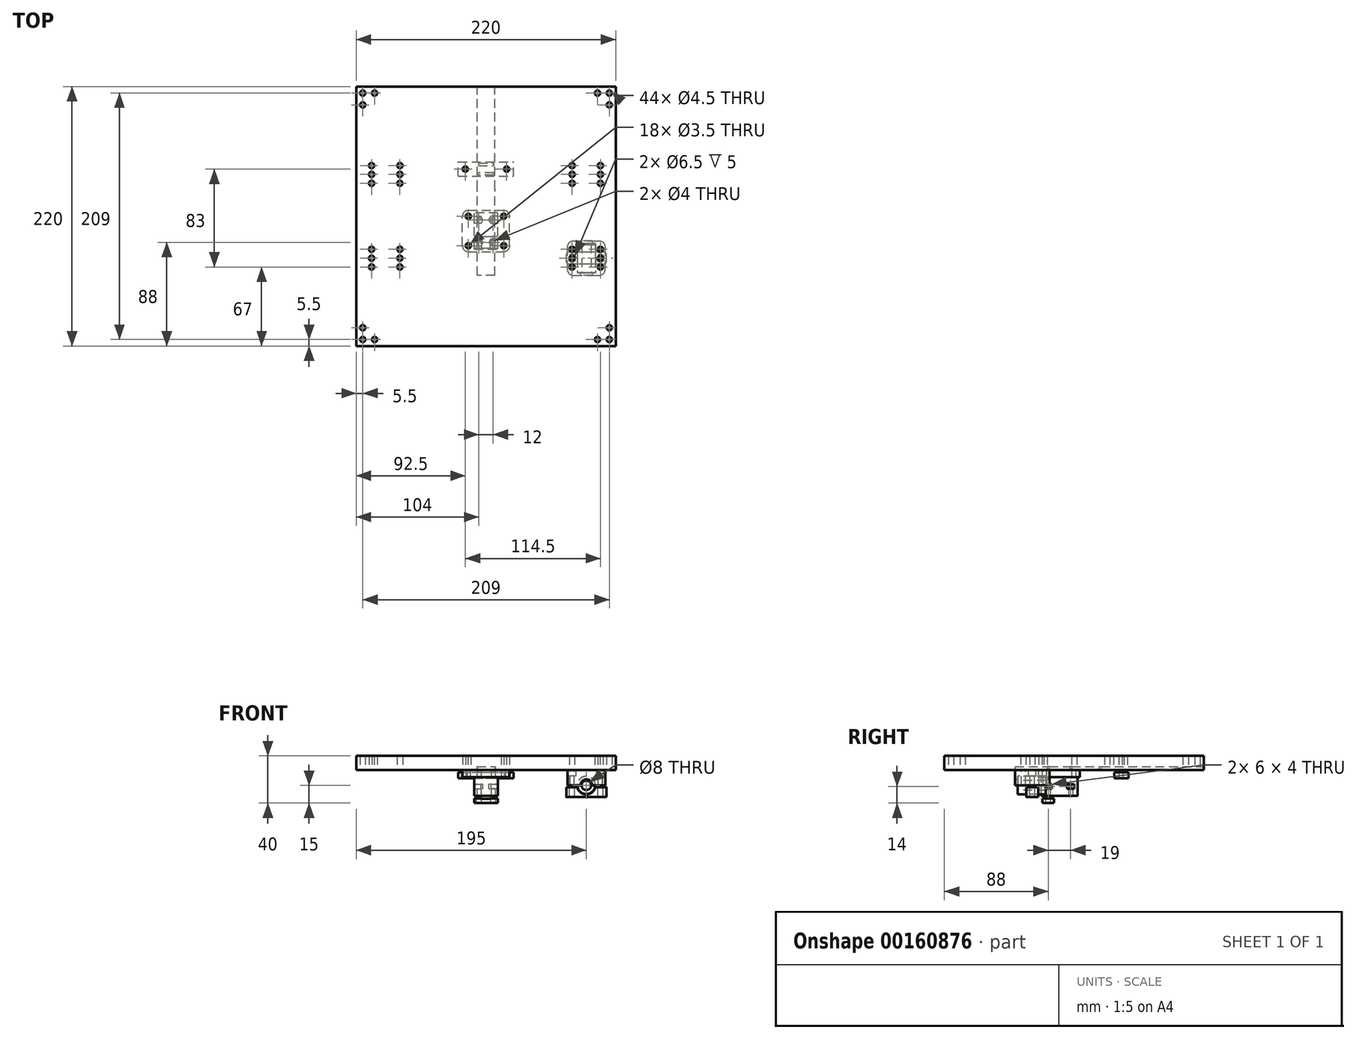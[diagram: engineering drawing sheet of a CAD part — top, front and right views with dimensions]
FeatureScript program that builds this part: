
annotation { "Feature Type Name" : "Feature", "Feature Type Description" : "" }
export const myFeature = defineFeature(function(context is Context, id is Id, definition is map)
    precondition{}
    {
        {
            var Q0;
            Q0=qCreatedBy(makeId("Top.planeOp"),FACE);
            var sketch = newSketch(context, id + "F0", { "sketchPlane" : qUnion([Q0])});
            skLineSegment(sketch, "E0.bottom", {"start": v(-110, 110) * mm, "end": v(110, 110) * mm});
            skLineSegment(sketch, "E0.top", {"start": v(-110, -110) * mm, "end": v(110, -110) * mm});
            skLineSegment(sketch, "E0.left", {"start": v(-110, 110) * mm, "end": v(-110, -110) * mm});
            skLineSegment(sketch, "E0.right", {"start": v(110, 110) * mm, "end": v(110, -110) * mm});
            skPoint(sketch, "E1", {"position": v(0, 110) * mm});
            skPoint(sketch, "E2", {"position": v(110, 0) * mm});
            skLineSegment(sketch, "E3", {"start": v(85, -48) * mm, "end": v(85, 0) * mm, "construction": true});
            skCircle(sketch, "E4", {"center": v(97, -43) * mm, "radius": 2.25 * mm});
            skLineSegment(sketch, "E5", {"start": v(85, -48) * mm, "end": v(92.5, -48) * mm, "construction": true});
            skLineSegment(sketch, "E6", {"start": v(92.5, -48) * mm, "end": v(92.5, -23) * mm, "construction": true});
            skLineSegment(sketch, "E7", {"start": v(92.5, -23) * mm, "end": v(77.5, -23) * mm, "construction": true});
            skLineSegment(sketch, "E8", {"start": v(77.5, -23) * mm, "end": v(77.5, -48) * mm, "construction": true});
            skLineSegment(sketch, "E9", {"start": v(77.5, -48) * mm, "end": v(85, -48) * mm, "construction": true});
            skLineSegment(sketch, "E10", {"start": v(77.5, -35.5) * mm, "end": v(92.5, -35.5) * mm, "construction": true});
            skCircle(sketch, "E11.MirrorC", {"center": v(97, -28) * mm, "radius": 2.25 * mm});
            skCircle(sketch, "E12.MirrorC", {"center": v(73, -28) * mm, "radius": 2.25 * mm});
            skCircle(sketch, "E13.MirrorC", {"center": v(73, -43) * mm, "radius": 2.25 * mm});
            skLineSegment(sketch, "E14", {"start": v(85, -48) * mm, "end": v(85, -50) * mm, "construction": true});
            skLineSegment(sketch, "E15.bottom", {"start": v(69, -50) * mm, "end": v(101, -50) * mm, "construction": true});
            skLineSegment(sketch, "E15.top", {"start": v(69, -21) * mm, "end": v(101, -21) * mm, "construction": true});
            skLineSegment(sketch, "E15.left", {"start": v(69, -50) * mm, "end": v(69, -21) * mm, "construction": true});
            skLineSegment(sketch, "E15.right", {"start": v(101, -50) * mm, "end": v(101, -21) * mm, "construction": true});
            skCircle(sketch, "E16", {"center": v(73, -35.5) * mm, "radius": 2.25 * mm});
            skCircle(sketch, "E17.MirrorC", {"center": v(97, -35.5) * mm, "radius": 2.25 * mm});
            skCircle(sketch, "E18.MirrorC", {"center": v(73, 28) * mm, "radius": 2.25 * mm});
            skCircle(sketch, "E19.MirrorC", {"center": v(73, 35.5) * mm, "radius": 2.25 * mm});
            skCircle(sketch, "E20.MirrorC", {"center": v(73, 43) * mm, "radius": 2.25 * mm});
            skCircle(sketch, "E21.MirrorC", {"center": v(97, 43) * mm, "radius": 2.25 * mm});
            skCircle(sketch, "E22.MirrorC", {"center": v(97, 35.5) * mm, "radius": 2.25 * mm});
            skCircle(sketch, "E23.MirrorC", {"center": v(97, 28) * mm, "radius": 2.25 * mm});
            skCircle(sketch, "E24.MirrorC", {"center": v(-73, 43) * mm, "radius": 2.25 * mm});
            skCircle(sketch, "E25.MirrorC", {"center": v(-73, 28) * mm, "radius": 2.25 * mm});
            skCircle(sketch, "E26.MirrorC", {"center": v(-97, 28) * mm, "radius": 2.25 * mm});
            skCircle(sketch, "E27.MirrorC", {"center": v(-97, 43) * mm, "radius": 2.25 * mm});
            skCircle(sketch, "E28.MirrorC", {"center": v(-73, 35.5) * mm, "radius": 2.25 * mm});
            skCircle(sketch, "E29.MirrorC", {"center": v(-97, 35.5) * mm, "radius": 2.25 * mm});
            skCircle(sketch, "E30.MirrorC", {"center": v(-73, -28) * mm, "radius": 2.25 * mm});
            skCircle(sketch, "E31.MirrorC", {"center": v(-73, -35.5) * mm, "radius": 2.25 * mm});
            skCircle(sketch, "E32.MirrorC", {"center": v(-73, -43) * mm, "radius": 2.25 * mm});
            skCircle(sketch, "E33.MirrorC", {"center": v(-97, -43) * mm, "radius": 2.25 * mm});
            skCircle(sketch, "E34.MirrorC", {"center": v(-97, -35.5) * mm, "radius": 2.25 * mm});
            skCircle(sketch, "E35.MirrorC", {"center": v(-97, -28) * mm, "radius": 2.25 * mm});
            skCircle(sketch, "E36", {"center": v(104.5, 104.5) * mm, "radius": 2.25 * mm});
            skCircle(sketch, "E37", {"center": v(104.5, 94.5) * mm, "radius": 2.25 * mm});
            skCircle(sketch, "E38.1.0", {"center": v(94.5, 104.5) * mm, "radius": 2.25 * mm});
            skLineSegment(sketch, "E38.anchor1", {"start": v(104.5, 104.5) * mm, "end": v(104.5, 94.5) * mm, "construction": true});
            skLineSegment(sketch, "E38.anchor2", {"start": v(104.5, 104.5) * mm, "end": v(94.5, 104.5) * mm, "construction": true});
            skCircle(sketch, "E39.MirrorC", {"center": v(104.5, -94.5) * mm, "radius": 2.25 * mm});
            skCircle(sketch, "E40.MirrorC", {"center": v(104.5, -104.5) * mm, "radius": 2.25 * mm});
            skCircle(sketch, "E41.MirrorC", {"center": v(94.5, -104.5) * mm, "radius": 2.25 * mm});
            skCircle(sketch, "E42.MirrorC", {"center": v(-94.5, -104.5) * mm, "radius": 2.25 * mm});
            skCircle(sketch, "E43.MirrorC", {"center": v(-104.5, -104.5) * mm, "radius": 2.25 * mm});
            skCircle(sketch, "E44.MirrorC", {"center": v(-104.5, -94.5) * mm, "radius": 2.25 * mm});
            skCircle(sketch, "E45.MirrorC", {"center": v(-104.5, 94.5) * mm, "radius": 2.25 * mm});
            skCircle(sketch, "E46.MirrorC", {"center": v(-104.5, 104.5) * mm, "radius": 2.25 * mm});
            skCircle(sketch, "E47.MirrorC", {"center": v(-94.5, 104.5) * mm, "radius": 2.25 * mm});
            skCircle(sketch, "E48.2.0.0", {"center": v(-17.5, 40) * mm, "radius": 2.25 * mm});
            skCircle(sketch, "E49.MirrorC", {"center": v(17.5, 40) * mm, "radius": 2.25 * mm});
            skCircle(sketch, "E50", {"center": v(-15, -25) * mm, "radius": 2.25 * mm});
            skCircle(sketch, "E51.MirrorC", {"center": v(15, -25) * mm, "radius": 2.25 * mm});
            skCircle(sketch, "E52", {"center": v(-15, 0) * mm, "radius": 2.25 * mm});
            skCircle(sketch, "E53.MirrorC", {"center": v(15, 0) * mm, "radius": 2.25 * mm});
            skSolve(sketch);
        }
        {
            var Q0;
            Q0 = qSketchRegion(id + "F0", true);
            extrude(context, id + "F1", {"entities" : qUnion([Q0]), "depth" : 12 * mm});
        }
        {
            var Q0;
            Q0=makeQuery(id+"F1.opExtrude","CAP_FACE",FACE,{"disambiguationData":[OSD([sQuery(id+"F0.wireOp",EDGE,"E0.bottom"),sQuery(id+"F0.wireOp",EDGE,"E0.top"),sQuery(id+"F0.wireOp",EDGE,"E0.left"),sQuery(id+"F0.wireOp",EDGE,"E0.right"),sQuery(id+"F0.wireOp",EDGE,"E4"),sQuery(id+"F0.wireOp",EDGE,"E11.MirrorC"),sQuery(id+"F0.wireOp",EDGE,"E12.MirrorC"),sQuery(id+"F0.wireOp",EDGE,"E13.MirrorC"),sQuery(id+"F0.wireOp",EDGE,"E16"),sQuery(id+"F0.wireOp",EDGE,"E17.MirrorC"),sQuery(id+"F0.wireOp",EDGE,"E18.MirrorC"),sQuery(id+"F0.wireOp",EDGE,"E19.MirrorC"),sQuery(id+"F0.wireOp",EDGE,"E20.MirrorC"),sQuery(id+"F0.wireOp",EDGE,"E21.MirrorC"),sQuery(id+"F0.wireOp",EDGE,"E22.MirrorC"),sQuery(id+"F0.wireOp",EDGE,"E23.MirrorC"),sQuery(id+"F0.wireOp",EDGE,"E24.MirrorC"),sQuery(id+"F0.wireOp",EDGE,"E25.MirrorC"),sQuery(id+"F0.wireOp",EDGE,"E26.MirrorC"),sQuery(id+"F0.wireOp",EDGE,"E27.MirrorC"),sQuery(id+"F0.wireOp",EDGE,"E28.MirrorC"),sQuery(id+"F0.wireOp",EDGE,"E29.MirrorC"),sQuery(id+"F0.wireOp",EDGE,"E30.MirrorC"),sQuery(id+"F0.wireOp",EDGE,"E31.MirrorC"),sQuery(id+"F0.wireOp",EDGE,"E32.MirrorC"),sQuery(id+"F0.wireOp",EDGE,"E33.MirrorC"),sQuery(id+"F0.wireOp",EDGE,"E34.MirrorC"),sQuery(id+"F0.wireOp",EDGE,"E35.MirrorC"),sQuery(id+"F0.wireOp",EDGE,"E36"),sQuery(id+"F0.wireOp",EDGE,"E37"),sQuery(id+"F0.wireOp",EDGE,"E38.1.0"),sQuery(id+"F0.wireOp",EDGE,"E39.MirrorC"),sQuery(id+"F0.wireOp",EDGE,"E40.MirrorC"),sQuery(id+"F0.wireOp",EDGE,"E41.MirrorC"),sQuery(id+"F0.wireOp",EDGE,"E42.MirrorC"),sQuery(id+"F0.wireOp",EDGE,"E43.MirrorC"),sQuery(id+"F0.wireOp",EDGE,"E44.MirrorC"),sQuery(id+"F0.wireOp",EDGE,"E45.MirrorC"),sQuery(id+"F0.wireOp",EDGE,"E46.MirrorC"),sQuery(id+"F0.wireOp",EDGE,"E47.MirrorC")])],"isStart":true});
            var sketch = newSketch(context, id + "F2", { "sketchPlane" : qUnion([Q0])});
            skLineSegment(sketch, "E54.right", {"start": v(7.5, 50) * mm, "end": v(7.5, -110) * mm});
            skLineSegment(sketch, "E55", {"start": v(-7.5, 50) * mm, "end": v(-7.5, -110) * mm});
            skLineSegment(sketch, "E56", {"start": v(-7.5, -110) * mm, "end": v(7.5, -110) * mm});
            skLineSegment(sketch, "E57", {"start": v(7.5, 50) * mm, "end": v(-7.5, 50) * mm});
            skPoint(sketch, "E58", {"position": v(0, 50) * mm});
            skSolve(sketch);
        }
        {
            var Q0;
            Q0 = qSketchRegion(id + "F2", true);
            extrude(context, id + "F3", {"entities" : qUnion([Q0]), "operationType" : NewBodyOperationType.REMOVE, "oppositeDirection" : true, "depth" : 3 * mm});
        }
        {
            var Q0;
            Q0=makeQuery(id+"F1.opExtrude","CAP_FACE",FACE,{"disambiguationData":[OSD([sQuery(id+"F0.wireOp",EDGE,"E0.bottom"),sQuery(id+"F0.wireOp",EDGE,"E0.top"),sQuery(id+"F0.wireOp",EDGE,"E0.left"),sQuery(id+"F0.wireOp",EDGE,"E0.right"),sQuery(id+"F0.wireOp",EDGE,"E4"),sQuery(id+"F0.wireOp",EDGE,"E11.MirrorC"),sQuery(id+"F0.wireOp",EDGE,"E12.MirrorC"),sQuery(id+"F0.wireOp",EDGE,"E13.MirrorC"),sQuery(id+"F0.wireOp",EDGE,"E16"),sQuery(id+"F0.wireOp",EDGE,"E17.MirrorC"),sQuery(id+"F0.wireOp",EDGE,"E18.MirrorC"),sQuery(id+"F0.wireOp",EDGE,"E19.MirrorC"),sQuery(id+"F0.wireOp",EDGE,"E20.MirrorC"),sQuery(id+"F0.wireOp",EDGE,"E21.MirrorC"),sQuery(id+"F0.wireOp",EDGE,"E22.MirrorC"),sQuery(id+"F0.wireOp",EDGE,"E23.MirrorC"),sQuery(id+"F0.wireOp",EDGE,"E24.MirrorC"),sQuery(id+"F0.wireOp",EDGE,"E25.MirrorC"),sQuery(id+"F0.wireOp",EDGE,"E26.MirrorC"),sQuery(id+"F0.wireOp",EDGE,"E27.MirrorC"),sQuery(id+"F0.wireOp",EDGE,"E28.MirrorC"),sQuery(id+"F0.wireOp",EDGE,"E29.MirrorC"),sQuery(id+"F0.wireOp",EDGE,"E30.MirrorC"),sQuery(id+"F0.wireOp",EDGE,"E31.MirrorC"),sQuery(id+"F0.wireOp",EDGE,"E32.MirrorC"),sQuery(id+"F0.wireOp",EDGE,"E33.MirrorC"),sQuery(id+"F0.wireOp",EDGE,"E34.MirrorC"),sQuery(id+"F0.wireOp",EDGE,"E35.MirrorC"),sQuery(id+"F0.wireOp",EDGE,"E36"),sQuery(id+"F0.wireOp",EDGE,"E37"),sQuery(id+"F0.wireOp",EDGE,"E38.1.0"),sQuery(id+"F0.wireOp",EDGE,"E39.MirrorC"),sQuery(id+"F0.wireOp",EDGE,"E40.MirrorC"),sQuery(id+"F0.wireOp",EDGE,"E41.MirrorC"),sQuery(id+"F0.wireOp",EDGE,"E42.MirrorC"),sQuery(id+"F0.wireOp",EDGE,"E43.MirrorC"),sQuery(id+"F0.wireOp",EDGE,"E44.MirrorC"),sQuery(id+"F0.wireOp",EDGE,"E45.MirrorC"),sQuery(id+"F0.wireOp",EDGE,"E46.MirrorC"),sQuery(id+"F0.wireOp",EDGE,"E47.MirrorC"),sQuery(id+"F0.wireOp",EDGE,"2d330509-3fee-4166-8db4-879286056b2e0.MirrorC"),sQuery(id+"F0.wireOp",EDGE,"E48.1.0.0"),sQuery(id+"F0.wireOp",EDGE,"E48.2.0.0"),sQuery(id+"F0.wireOp",EDGE,"9dcae126-daf7-457d-810f-363c11d3aa460.MirrorC"),sQuery(id+"F0.wireOp",EDGE,"9b4604d9-289c-45bc-b21d-af252c6502e40.MirrorC"),sQuery(id+"F0.wireOp",EDGE,"E49.MirrorC")])],"isStart":true});
            cPlane(context, id + "F4", {"entities" : qUnion([Q0]), "cplaneType" : CPlaneType.OFFSET, "offset" : 2 * mm, "width" : 150 * mm, "height" : 150 * mm});
        }
        {
            var Q0;
            Q0=qCreatedBy(id+"F4.planeOp",FACE);
            var sketch = newSketch(context, id + "F5", { "sketchPlane" : qUnion([Q0])});
            skCircle(sketch, "E59", {"center": v(17.5, -40) * mm, "radius": 1.75 * mm});
            skLineSegment(sketch, "E60.bottom", {"start": v(-23.5, -34) * mm, "end": v(23.5, -34) * mm});
            skLineSegment(sketch, "E60.top", {"start": v(-23.5, -46) * mm, "end": v(23.5, -46) * mm});
            skLineSegment(sketch, "E60.left", {"start": v(-23.5, -34) * mm, "end": v(-23.5, -46) * mm});
            skLineSegment(sketch, "E60.right", {"start": v(23.5, -34) * mm, "end": v(23.5, -46) * mm});
            skPoint(sketch, "E61", {"position": v(23.5, -40) * mm});
            skPoint(sketch, "E62", {"position": v(0, -34) * mm});
            skLineSegment(sketch, "E63", {"start": v(0, -34) * mm, "end": v(0, -46) * mm, "construction": true});
            skCircle(sketch, "E64.MirrorC", {"center": v(-17.5, -40) * mm, "radius": 1.75 * mm});
            skSolve(sketch);
        }
        {
            var Q0;
            Q0 = qSketchRegion(id + "F5", true);
            extrude(context, id + "F6", {"entities" : qUnion([Q0]), "depth" : 5 * mm});
        }
        {
            var Q0;
            Q0=makeQuery(id+"F6.opExtrude","CAP_FACE",FACE,{"disambiguationData":[OSD([sQuery(id+"F5.wireOp",EDGE,"E59"),sQuery(id+"F5.wireOp",EDGE,"E60.bottom"),sQuery(id+"F5.wireOp",EDGE,"E60.top"),sQuery(id+"F5.wireOp",EDGE,"E60.left"),sQuery(id+"F5.wireOp",EDGE,"E60.right"),sQuery(id+"F5.wireOp",EDGE,"E64.MirrorC")])],"isStart":true});
            var sketch = newSketch(context, id + "F7", { "sketchPlane" : qUnion([Q0])});
            skLineSegment(sketch, "E65.bottom", {"start": v(-7.5, 46) * mm, "end": v(7.5, 46) * mm, "construction": true});
            skLineSegment(sketch, "E65.top", {"start": v(-7.5, 34) * mm, "end": v(7.5, 34) * mm, "construction": true});
            skLineSegment(sketch, "E65.left", {"start": v(-7.5, 46) * mm, "end": v(-7.5, 34) * mm, "construction": true});
            skLineSegment(sketch, "E65.right", {"start": v(7.5, 46) * mm, "end": v(7.5, 34) * mm, "construction": true});
            skPoint(sketch, "E66", {"position": v(0, 46) * mm});
            skLineSegment(sketch, "E67", {"start": v(0, 45) * mm, "end": v(6.5, 45) * mm});
            skLineSegment(sketch, "E68", {"start": v(6.5, 45) * mm, "end": v(6.5, 43) * mm});
            skLineSegment(sketch, "E69", {"start": v(6.5, 43) * mm, "end": v(0, 43) * mm});
            skLineSegment(sketch, "E70", {"start": v(7.5, 40) * mm, "end": v(-7.5, 40) * mm, "construction": true});
            skLineSegment(sketch, "E71.MirrorCS", {"start": v(0, 45) * mm, "end": v(-6.5, 45) * mm});
            skLineSegment(sketch, "E72.MirrorCS", {"start": v(-6.5, 45) * mm, "end": v(-6.5, 43) * mm});
            skLineSegment(sketch, "E73.MirrorCS", {"start": v(-6.5, 43) * mm, "end": v(0, 43) * mm});
            skLineSegment(sketch, "E74.MirrorCS", {"start": v(6.5, 37) * mm, "end": v(0, 37) * mm});
            skLineSegment(sketch, "E75.MirrorCS", {"start": v(6.5, 35) * mm, "end": v(6.5, 37) * mm});
            skLineSegment(sketch, "E76.MirrorCS", {"start": v(0, 35) * mm, "end": v(6.5, 35) * mm});
            skLineSegment(sketch, "E77.MirrorCS", {"start": v(0, 35) * mm, "end": v(-6.5, 35) * mm});
            skLineSegment(sketch, "E78.MirrorCS", {"start": v(-6.5, 37) * mm, "end": v(0, 37) * mm});
            skLineSegment(sketch, "E79.MirrorCS", {"start": v(-6.5, 35) * mm, "end": v(-6.5, 37) * mm});
            skSolve(sketch);
        }
        {
            var Q0;
            Q0 = qSketchRegion(id + "F7", true);
            extrude(context, id + "F8", {"entities" : qUnion([Q0]), "operationType" : NewBodyOperationType.ADD, "depth" : 2 * mm});
        }
        {
            var Q0;
            Q0=qCreatedBy(makeId("Top.planeOp"),FACE);
            var sketch = newSketch(context, id + "F9", { "sketchPlane" : qUnion([Q0])});
            skLineSegment(sketch, "E80", {"start": v(85, -48) * mm, "end": v(85, 0) * mm, "construction": true});
            skCircle(sketch, "E81", {"center": v(97, -43) * mm, "radius": 1.75 * mm});
            skLineSegment(sketch, "E82", {"start": v(85, -48) * mm, "end": v(92.5, -48) * mm, "construction": true});
            skLineSegment(sketch, "E83", {"start": v(92.5, -48) * mm, "end": v(92.5, -23) * mm, "construction": true});
            skLineSegment(sketch, "E84", {"start": v(92.5, -23) * mm, "end": v(77.5, -23) * mm, "construction": true});
            skLineSegment(sketch, "E85", {"start": v(77.5, -23) * mm, "end": v(77.5, -48) * mm, "construction": true});
            skLineSegment(sketch, "E86", {"start": v(77.5, -48) * mm, "end": v(85, -48) * mm, "construction": true});
            skLineSegment(sketch, "E87", {"start": v(92.5, -35.5) * mm, "end": v(103.36, -35.5) * mm, "construction": true});
            skCircle(sketch, "E88.MirrorC", {"center": v(97, -28) * mm, "radius": 1.75 * mm});
            skCircle(sketch, "E89.MirrorC", {"center": v(73, -28) * mm, "radius": 1.75 * mm});
            skCircle(sketch, "E90.MirrorC", {"center": v(73, -43) * mm, "radius": 1.75 * mm});
            skLineSegment(sketch, "E91", {"start": v(85, -48) * mm, "end": v(85, -50) * mm, "construction": true});
            skLineSegment(sketch, "E92.bottom", {"start": v(74, -50) * mm, "end": v(96, -50) * mm});
            skLineSegment(sketch, "E92.top", {"start": v(74, -21) * mm, "end": v(96, -21) * mm});
            skLineSegment(sketch, "E92.left", {"start": v(69, -45) * mm, "end": v(69, -26) * mm});
            skLineSegment(sketch, "E92.right", {"start": v(101, -45) * mm, "end": v(101, -26) * mm});
            skCircle(sketch, "E93", {"center": v(73, -35.5) * mm, "radius": 1.9 * mm});
            skCircle(sketch, "E94.MirrorC", {"center": v(97, -35.5) * mm, "radius": 1.9 * mm});
            skPoint(sketch, "E95.visualSharp", {"position": v(101, -50) * mm});
            skArc(sketch, "E95.filletArc", {"start": v(96, -50) * mm, "mid": v(99.54, -48.54) * mm, "end": v(101, -45) * mm});
            skPoint(sketch, "E96.visualSharp", {"position": v(69, -21) * mm});
            skArc(sketch, "E96.filletArc", {"start": v(74, -21) * mm, "mid": v(70.46, -22.46) * mm, "end": v(69, -26) * mm});
            skPoint(sketch, "E97.visualSharp", {"position": v(101, -21) * mm});
            skArc(sketch, "E97.filletArc", {"start": v(101, -26) * mm, "mid": v(99.54, -22.46) * mm, "end": v(96, -21) * mm});
            skPoint(sketch, "E98.visualSharp", {"position": v(69, -50) * mm});
            skArc(sketch, "E98.filletArc", {"start": v(69, -45) * mm, "mid": v(70.46, -48.54) * mm, "end": v(74, -50) * mm});
            skSolve(sketch);
        }
        {
            var Q0;
            Q0 = qSketchRegion(id + "F9", true);
            extrude(context, id + "F10", {"entities" : qUnion([Q0]), "oppositeDirection" : true, "depth" : 13 * mm});
        }
        {
            var Q0;
            Q0=makeQuery(id+"F10.opExtrude","CAP_FACE",FACE,{"disambiguationData":[OSD([sQuery(id+"F9.wireOp",EDGE,"E81"),sQuery(id+"F9.wireOp",EDGE,"E88.MirrorC"),sQuery(id+"F9.wireOp",EDGE,"E89.MirrorC"),sQuery(id+"F9.wireOp",EDGE,"E90.MirrorC"),sQuery(id+"F9.wireOp",EDGE,"E92.bottom"),sQuery(id+"F9.wireOp",EDGE,"E92.top"),sQuery(id+"F9.wireOp",EDGE,"E92.left"),sQuery(id+"F9.wireOp",EDGE,"E92.right"),sQuery(id+"F9.wireOp",EDGE,"E93"),sQuery(id+"F9.wireOp",EDGE,"E94.MirrorC")])],"isStart":true});
            var sketch = newSketch(context, id + "F11", { "sketchPlane" : qUnion([Q0])});
            skCircle(sketch, "E99", {"center": v(97, -35.5) * mm, "radius": 3.25 * mm});
            skLineSegment(sketch, "E100", {"start": v(85, -21) * mm, "end": v(85, -50) * mm, "construction": true});
            skCircle(sketch, "E101.MirrorC", {"center": v(73, -35.5) * mm, "radius": 3.25 * mm});
            skSolve(sketch);
        }
        {
            var Q0;
            Q0 = qSketchRegion(id + "F11", true);
            extrude(context, id + "F12", {"entities" : qUnion([Q0]), "operationType" : NewBodyOperationType.REMOVE, "oppositeDirection" : true, "depth" : 5 * mm});
        }
        {
            var Q0;
            Q0=makeQuery(id+"F10.opExtrude","SWEPT_FACE",FACE,{"disambiguationData":[OSD([sQuery(id+"F9.wireOp",EDGE,"E92.bottom")])]});
            var sketch = newSketch(context, id + "F13", { "sketchPlane" : qUnion([Q0])});
            skCircle(sketch, "E102", {"center": v(85, -13) * mm, "radius": 5 * mm});
            skPoint(sketch, "E103", {"position": v(85, 0) * mm});
            skSolve(sketch);
        }
        {
            var Q0;
            Q0 = qSketchRegion(id + "F13", true);
            extrude(context, id + "F14", {"entities" : qUnion([Q0]), "operationType" : NewBodyOperationType.REMOVE, "oppositeDirection" : true, "depth" : 30 * mm});
        }
        {
            var Q0;
            {var subQ0=sQuery(id+"F9.wireOp",EDGE,"E92.top");var subQ1=sQuery(id+"F9.wireOp",EDGE,"E92.bottom");var subQ2=sQuery(id+"F9.wireOp",EDGE,"E88.MirrorC");var subQ3=sQuery(id+"F9.wireOp",EDGE,"E81");var subQ4=sQuery(id+"F9.wireOp",EDGE,"E94.MirrorC");var subQ5=sQuery(id+"F9.wireOp",EDGE,"E92.right");Q0=makeQuery(id+"F14.boolean.opBoolean","SPLIT",FACE,{"disambiguationData":[TD([makeQuery(id+"F10.opExtrude","SWEPT_FACE",FACE,{"disambiguationData":[OSD([subQ3])]})])],"derivedFrom":makeQuery(id+"F10.opExtrude","CAP_FACE",FACE,{"disambiguationData":[OSD([subQ3,subQ2,sQuery(id+"F9.wireOp",EDGE,"E89.MirrorC"),sQuery(id+"F9.wireOp",EDGE,"E90.MirrorC"),subQ1,subQ0,sQuery(id+"F9.wireOp",EDGE,"E92.left"),subQ5,sQuery(id+"F9.wireOp",EDGE,"E93"),subQ4])],"isStart":false})});}
            var sketch = newSketch(context, id + "F15", { "sketchPlane" : qUnion([Q0])});
            skPoint(sketch, "E104", {"position": v(97, 35.5) * mm});
            skPoint(sketch, "E105", {"position": v(73, 35.5) * mm});
            skCircle(sketch, "E106", {"center": v(73, 35.5) * mm, "radius": 2.25 * mm});
            skCircle(sketch, "E107", {"center": v(97, 35.5) * mm, "radius": 2.25 * mm});
            skLineSegment(sketch, "E108", {"start": v(73, 35.5) * mm, "end": v(97, 35.5) * mm, "construction": true});
            skLineSegment(sketch, "E109", {"start": v(85, 35.5) * mm, "end": v(85, 38.53) * mm, "construction": true});
            skArc(sketch, "E110", {"start": v(102, 38.5) * mm, "mid": v(101.41, 39.91) * mm, "end": v(100, 40.5) * mm});
            skLineSegment(sketch, "E111", {"start": v(100, 40.5) * mm, "end": v(85, 40.5) * mm});
            skLineSegment(sketch, "E112.MirrorCS", {"start": v(70, 40.5) * mm, "end": v(85, 40.5) * mm});
            skArc(sketch, "E113.MirrorCS", {"start": v(68, 38.5) * mm, "mid": v(68.59, 39.91) * mm, "end": v(70, 40.5) * mm});
            skArc(sketch, "E114.MirrorCS", {"start": v(68, 32.5) * mm, "mid": v(68.59, 31.09) * mm, "end": v(70, 30.5) * mm});
            skLineSegment(sketch, "E115.MirrorCS", {"start": v(70, 30.5) * mm, "end": v(85, 30.5) * mm});
            skLineSegment(sketch, "E116.MirrorCS", {"start": v(100, 30.5) * mm, "end": v(85, 30.5) * mm});
            skArc(sketch, "E117.MirrorCS", {"start": v(102, 32.5) * mm, "mid": v(101.41, 31.09) * mm, "end": v(100, 30.5) * mm});
            skLineSegment(sketch, "E118", {"start": v(102, 38.5) * mm, "end": v(102, 32.5) * mm});
            skLineSegment(sketch, "E119.MirrorCS", {"start": v(68, 38.5) * mm, "end": v(68, 32.5) * mm});
            skSolve(sketch);
        }
        {
            var Q0;
            Q0 = qSketchRegion(id + "F15", true);
            extrude(context, id + "F16", {"entities" : qUnion([Q0]), "depth" : 10 * mm, "hasSecondDirection" : true, "secondDirectionOppositeDirection" : false, "secondDirectionDepth" : 1.5 * mm});
        }
        {
            var Q0;
            Q0=makeQuery(id+"F10.opExtrude","SWEPT_FACE",FACE,{"disambiguationData":[OSD([sQuery(id+"F9.wireOp",EDGE,"E92.bottom")])]});
            var sketch = newSketch(context, id + "F17", { "sketchPlane" : qUnion([Q0])});
            skCircle(sketch, "E120", {"center": v(85, -13) * mm, "radius": 7.75 * mm});
            skSolve(sketch);
        }
        {
            var Q0;
            Q0 = qSketchRegion(id + "F17", true);
            extrude(context, id + "F18", {"entities" : qUnion([Q0]), "operationType" : NewBodyOperationType.REMOVE, "oppositeDirection" : true, "depth" : 27 * mm, "hasSecondDirection" : true, "secondDirectionOppositeDirection" : true, "secondDirectionDepth" : 2 * mm});
        }
        {
            var Q0;
            Q0=makeQuery(id+"F18.boolean.opBoolean","COPY",FACE,{"derivedFrom":makeQuery(id+"F18.opExtrude","CAP_FACE",FACE,{"disambiguationData":[OSD([sQuery(id+"F17.wireOp",EDGE,"E120")])],"isStart":true})});
            var sketch = newSketch(context, id + "F19", { "sketchPlane" : qUnion([Q0])});
            skCircle(sketch, "E121", {"center": v(-85, -13) * mm, "radius": 7.5 * mm});
            skCircle(sketch, "E122", {"center": v(-85, -13) * mm, "radius": 4 * mm});
            skSolve(sketch);
        }
        {
            var Q0;
            Q0 = qSketchRegion(id + "F19", true);
            extrude(context, id + "F20", {"entities" : qUnion([Q0]), "depth" : 24 * mm});
        }
        {
            var Q0;
            Q0=makeQuery(id+"F1.opExtrude","CAP_FACE",FACE,{"disambiguationData":[OSD([sQuery(id+"F0.wireOp",EDGE,"E0.bottom"),sQuery(id+"F0.wireOp",EDGE,"E0.top"),sQuery(id+"F0.wireOp",EDGE,"E0.left"),sQuery(id+"F0.wireOp",EDGE,"E0.right"),sQuery(id+"F0.wireOp",EDGE,"E4"),sQuery(id+"F0.wireOp",EDGE,"E11.MirrorC"),sQuery(id+"F0.wireOp",EDGE,"E12.MirrorC"),sQuery(id+"F0.wireOp",EDGE,"E13.MirrorC"),sQuery(id+"F0.wireOp",EDGE,"E16"),sQuery(id+"F0.wireOp",EDGE,"E17.MirrorC"),sQuery(id+"F0.wireOp",EDGE,"E18.MirrorC"),sQuery(id+"F0.wireOp",EDGE,"E19.MirrorC"),sQuery(id+"F0.wireOp",EDGE,"E20.MirrorC"),sQuery(id+"F0.wireOp",EDGE,"E21.MirrorC"),sQuery(id+"F0.wireOp",EDGE,"E22.MirrorC"),sQuery(id+"F0.wireOp",EDGE,"E23.MirrorC"),sQuery(id+"F0.wireOp",EDGE,"E24.MirrorC"),sQuery(id+"F0.wireOp",EDGE,"E25.MirrorC"),sQuery(id+"F0.wireOp",EDGE,"E26.MirrorC"),sQuery(id+"F0.wireOp",EDGE,"E27.MirrorC"),sQuery(id+"F0.wireOp",EDGE,"E28.MirrorC"),sQuery(id+"F0.wireOp",EDGE,"E29.MirrorC"),sQuery(id+"F0.wireOp",EDGE,"E30.MirrorC"),sQuery(id+"F0.wireOp",EDGE,"E31.MirrorC"),sQuery(id+"F0.wireOp",EDGE,"E32.MirrorC"),sQuery(id+"F0.wireOp",EDGE,"E33.MirrorC"),sQuery(id+"F0.wireOp",EDGE,"E34.MirrorC"),sQuery(id+"F0.wireOp",EDGE,"E35.MirrorC"),sQuery(id+"F0.wireOp",EDGE,"E36"),sQuery(id+"F0.wireOp",EDGE,"E37"),sQuery(id+"F0.wireOp",EDGE,"E38.1.0"),sQuery(id+"F0.wireOp",EDGE,"E39.MirrorC"),sQuery(id+"F0.wireOp",EDGE,"E40.MirrorC"),sQuery(id+"F0.wireOp",EDGE,"E41.MirrorC"),sQuery(id+"F0.wireOp",EDGE,"E42.MirrorC"),sQuery(id+"F0.wireOp",EDGE,"E43.MirrorC"),sQuery(id+"F0.wireOp",EDGE,"E44.MirrorC"),sQuery(id+"F0.wireOp",EDGE,"E45.MirrorC"),sQuery(id+"F0.wireOp",EDGE,"E46.MirrorC"),sQuery(id+"F0.wireOp",EDGE,"E47.MirrorC"),sQuery(id+"F0.wireOp",EDGE,"E48.2.0.0"),sQuery(id+"F0.wireOp",EDGE,"E49.MirrorC"),sQuery(id+"F0.wireOp",EDGE,"E50"),sQuery(id+"F0.wireOp",EDGE,"E51.MirrorC"),sQuery(id+"F0.wireOp",EDGE,"d57d043d-9cb5-43e3-8a3d-f01461bb8ceb0.MirrorC"),sQuery(id+"F0.wireOp",EDGE,"eb3f84ab-b30f-4da7-bc09-f43ee8a39d940.MirrorC")])],"isStart":true});
            var sketch = newSketch(context, id + "F21", { "sketchPlane" : qUnion([Q0])});
            skLineSegment(sketch, "E123.bottom", {"start": v(-15, 30) * mm, "end": v(15, 30) * mm});
            skLineSegment(sketch, "E123.top", {"start": v(-15, -5) * mm, "end": v(15, -5) * mm});
            skLineSegment(sketch, "E123.left", {"start": v(-20, 25) * mm, "end": v(-20, 0) * mm});
            skLineSegment(sketch, "E123.right", {"start": v(20, 25) * mm, "end": v(20, 0) * mm});
            skPoint(sketch, "E124", {"position": v(0, 30) * mm});
            skPoint(sketch, "E125", {"position": v(20, 12.5) * mm});
            skCircle(sketch, "E126.MirrorC", {"center": v(-15, 25) * mm, "radius": 1.75 * mm});
            skCircle(sketch, "E127.MirrorC", {"center": v(15, 25) * mm, "radius": 1.75 * mm});
            skPoint(sketch, "E128.visualSharp", {"position": v(20, 30) * mm});
            skArc(sketch, "E128.filletArc", {"start": v(20, 25) * mm, "mid": v(18.54, 28.54) * mm, "end": v(15, 30) * mm});
            skPoint(sketch, "E129.visualSharp", {"position": v(-20, 30) * mm});
            skArc(sketch, "E129.filletArc", {"start": v(-15, 30) * mm, "mid": v(-18.54, 28.54) * mm, "end": v(-20, 25) * mm});
            skPoint(sketch, "E130.visualSharp", {"position": v(-20, -5) * mm});
            skArc(sketch, "E130.filletArc", {"start": v(-20, 0) * mm, "mid": v(-18.54, -3.54) * mm, "end": v(-15, -5) * mm});
            skPoint(sketch, "E131.visualSharp", {"position": v(20, -5) * mm});
            skArc(sketch, "E131.filletArc", {"start": v(15, -5) * mm, "mid": v(18.54, -3.54) * mm, "end": v(20, 0) * mm});
            skLineSegment(sketch, "E132", {"start": v(20, 12.5) * mm, "end": v(-20, 12.5) * mm, "construction": true});
            skCircle(sketch, "E133.MirrorC", {"center": v(-15, 0) * mm, "radius": 1.75 * mm});
            skCircle(sketch, "E134.MirrorC", {"center": v(15, 0) * mm, "radius": 1.75 * mm});
            skSolve(sketch);
        }
        {
            var Q0;
            Q0 = qSketchRegion(id + "F21", true);
            extrude(context, id + "F22", {"entities" : qUnion([Q0]), "depth" : 6 * mm});
        }
        {
            var Q0;
            Q0=makeQuery(id+"F22.opExtrude","CAP_FACE",FACE,{"disambiguationData":[OSD([sQuery(id+"F21.wireOp",EDGE,"E123.bottom"),sQuery(id+"F21.wireOp",EDGE,"E123.top"),sQuery(id+"F21.wireOp",EDGE,"E123.left"),sQuery(id+"F21.wireOp",EDGE,"E123.right"),sQuery(id+"F21.wireOp",EDGE,"HCweQ12N-9rIO-LCz3-vBci-XHL5mO5NlAkN"),sQuery(id+"F21.wireOp",EDGE,"843c52e2-a724-4464-8be3-4ee659ba84dc0.MirrorC"),sQuery(id+"F21.wireOp",EDGE,"E126.MirrorC"),sQuery(id+"F21.wireOp",EDGE,"E127.MirrorC"),sQuery(id+"F21.wireOp",EDGE,"E128.filletArc"),sQuery(id+"F21.wireOp",EDGE,"E129.filletArc"),sQuery(id+"F21.wireOp",EDGE,"E130.filletArc"),sQuery(id+"F21.wireOp",EDGE,"E131.filletArc")])],"isStart":false});
            var sketch = newSketch(context, id + "F23", { "sketchPlane" : qUnion([Q0])});
            skLineSegment(sketch, "E135.bottom", {"start": v(-10, 28) * mm, "end": v(10, 28) * mm});
            skLineSegment(sketch, "E135.left", {"start": v(-10, 28) * mm, "end": v(-10, -3) * mm});
            skLineSegment(sketch, "E135.right", {"start": v(10, 28) * mm, "end": v(10, -3) * mm});
            skLineSegment(sketch, "E136", {"start": v(10, -3) * mm, "end": v(-10, -3) * mm});
            skPoint(sketch, "E137", {"position": v(0, -3) * mm});
            skLineSegment(sketch, "E138", {"start": v(-102.57, -50) * mm, "end": v(101.86, -50) * mm, "construction": true});
            skLineSegment(sketch, "E139.MirrorCS", {"start": v(-102.57, 50) * mm, "end": v(101.86, 50) * mm, "construction": true});
            skSolve(sketch);
        }
        {
            var Q0;
            Q0 = qSketchRegion(id + "F23", true);
            extrude(context, id + "F24", {"entities" : qUnion([Q0]), "operationType" : NewBodyOperationType.ADD, "depth" : 16 * mm});
        }
        {
            var Q0;
            Q0=makeQuery(id+"F24.opExtrude","CAP_FACE",FACE,{"disambiguationData":[OSD([sQuery(id+"F23.wireOp",EDGE,"E135.bottom"),sQuery(id+"F23.wireOp",EDGE,"E135.top"),sQuery(id+"F23.wireOp",EDGE,"E135.left"),sQuery(id+"F23.wireOp",EDGE,"E135.right")])],"isStart":false});
            var sketch = newSketch(context, id + "F25", { "sketchPlane" : qUnion([Q0])});
            skCircle(sketch, "E140", {"center": v(6, 22) * mm, "radius": 1.75 * mm});
            skCircle(sketch, "E141.MirrorC", {"center": v(-6, 22) * mm, "radius": 1.75 * mm});
            skCircle(sketch, "E142.MirrorC", {"center": v(-6, -22) * mm, "radius": 1.75 * mm});
            skCircle(sketch, "E143.MirrorC", {"center": v(6, -22) * mm, "radius": 1.75 * mm});
            skLineSegment(sketch, "E144", {"start": v(10, 12.5) * mm, "end": v(-10, 12.5) * mm, "construction": true});
            skCircle(sketch, "E145.MirrorC", {"center": v(6, 3) * mm, "radius": 1.75 * mm});
            skCircle(sketch, "E146.MirrorC", {"center": v(-6, 3) * mm, "radius": 1.75 * mm});
            skSolve(sketch);
        }
        {
            var Q0;
            Q0 = qSketchRegion(id + "F25", true);
            extrude(context, id + "F26", {"entities" : qUnion([Q0]), "operationType" : NewBodyOperationType.REMOVE, "oppositeDirection" : true, "depth" : 25 * mm});
        }
        {
            var Q0;
            {var subQ0=sQuery(id+"F21.wireOp",EDGE,"843c52e2-a724-4464-8be3-4ee659ba84dc0.MirrorC");var subQ1=sQuery(id+"F21.wireOp",EDGE,"E123.right");var subQ2=sQuery(id+"F21.wireOp",EDGE,"E123.bottom");var subQ3=sQuery(id+"F21.wireOp",EDGE,"E123.top");var subQ4=sQuery(id+"F21.wireOp",EDGE,"E127.MirrorC");var subQ5=sQuery(id+"F21.wireOp",EDGE,"E128.filletArc");var subQ6=sQuery(id+"F21.wireOp",EDGE,"E131.filletArc");Q0=makeQuery(id+"F24.boolean.opBoolean","SPLIT",FACE,{"disambiguationData":[TD([makeQuery(id+"F22.opExtrude","SWEPT_FACE",FACE,{"disambiguationData":[OSD([subQ1])]})])],"derivedFrom":makeQuery(id+"F22.opExtrude","CAP_FACE",FACE,{"disambiguationData":[OSD([subQ2,subQ3,sQuery(id+"F21.wireOp",EDGE,"E123.left"),subQ1,sQuery(id+"F21.wireOp",EDGE,"HCweQ12N-9rIO-LCz3-vBci-XHL5mO5NlAkN"),subQ0,sQuery(id+"F21.wireOp",EDGE,"E126.MirrorC"),subQ4,subQ5,sQuery(id+"F21.wireOp",EDGE,"E129.filletArc"),sQuery(id+"F21.wireOp",EDGE,"E130.filletArc"),subQ6])],"isStart":false})});}
            var sketch = newSketch(context, id + "F27", { "sketchPlane" : qUnion([Q0])});
            skCircle(sketch, "E147.cCircle", {"center": v(6, 22) * mm, "radius": 3 * mm, "construction": true});
            skLineSegment(sketch, "E147.0", {"start": v(2.54, 22) * mm, "end": v(4.27, 25) * mm});
            skLineSegment(sketch, "E147.1", {"start": v(4.27, 25) * mm, "end": v(7.73, 25) * mm});
            skLineSegment(sketch, "E147.4", {"start": v(7.73, 19) * mm, "end": v(4.27, 19) * mm});
            skLineSegment(sketch, "E147.5", {"start": v(4.27, 19) * mm, "end": v(2.54, 22) * mm});
            skPoint(sketch, "E147.0.midPoint", {"position": v(3.4, 23.5) * mm});
            skLineSegment(sketch, "E148", {"start": v(7.73, 19) * mm, "end": v(27.28, 19) * mm});
            skLineSegment(sketch, "E149", {"start": v(27.28, 19) * mm, "end": v(27.28, 25) * mm});
            skLineSegment(sketch, "E150", {"start": v(27.28, 25) * mm, "end": v(7.73, 25) * mm});
            skLineSegment(sketch, "E151.MirrorCS", {"start": v(-4.27, 19) * mm, "end": v(-2.54, 22) * mm});
            skLineSegment(sketch, "E152.MirrorCS", {"start": v(-2.54, 22) * mm, "end": v(-4.27, 25) * mm});
            skLineSegment(sketch, "E153.MirrorCS", {"start": v(-4.27, 25) * mm, "end": v(-7.73, 25) * mm});
            skLineSegment(sketch, "E154.MirrorCS", {"start": v(-27.28, 25) * mm, "end": v(-7.73, 25) * mm});
            skLineSegment(sketch, "E155.MirrorCS", {"start": v(-27.28, 19) * mm, "end": v(-27.28, 25) * mm});
            skLineSegment(sketch, "E156.MirrorCS", {"start": v(-7.73, 19) * mm, "end": v(-27.28, 19) * mm});
            skLineSegment(sketch, "E157.MirrorCS", {"start": v(-7.73, 19) * mm, "end": v(-4.27, 19) * mm});
            skLineSegment(sketch, "E158", {"start": v(10, 12.5) * mm, "end": v(-10, 12.5) * mm, "construction": true});
            skLineSegment(sketch, "E159.MirrorCS", {"start": v(-4.27, 6) * mm, "end": v(-2.54, 3) * mm});
            skLineSegment(sketch, "E160.MirrorCS", {"start": v(-2.54, 3) * mm, "end": v(-4.27, 0) * mm});
            skLineSegment(sketch, "E161.MirrorCS", {"start": v(-4.27, 0) * mm, "end": v(-7.73, 0) * mm});
            skLineSegment(sketch, "E162.MirrorCS", {"start": v(-27.28, 0) * mm, "end": v(-7.73, 0) * mm});
            skLineSegment(sketch, "E163.MirrorCS", {"start": v(-27.28, 6) * mm, "end": v(-27.28, 0) * mm});
            skLineSegment(sketch, "E164.MirrorCS", {"start": v(-7.73, 6) * mm, "end": v(-27.28, 6) * mm});
            skLineSegment(sketch, "E165.MirrorCS", {"start": v(-7.73, 6) * mm, "end": v(-4.27, 6) * mm});
            skLineSegment(sketch, "E166.MirrorCS", {"start": v(4.27, 6) * mm, "end": v(2.54, 3) * mm});
            skLineSegment(sketch, "E167.MirrorCS", {"start": v(2.54, 3) * mm, "end": v(4.27, 0) * mm});
            skLineSegment(sketch, "E168.MirrorCS", {"start": v(4.27, 0) * mm, "end": v(7.73, 0) * mm});
            skLineSegment(sketch, "E169.MirrorCS", {"start": v(7.73, 6) * mm, "end": v(4.27, 6) * mm});
            skLineSegment(sketch, "E170.MirrorCS", {"start": v(7.73, 6) * mm, "end": v(27.28, 6) * mm});
            skLineSegment(sketch, "E171.MirrorCS", {"start": v(27.28, 0) * mm, "end": v(7.73, 0) * mm});
            skLineSegment(sketch, "E172.MirrorCS", {"start": v(27.28, 6) * mm, "end": v(27.28, 0) * mm});
            skSolve(sketch);
        }
        {
            var Q0;
            Q0 = qSketchRegion(id + "F27", true);
            extrude(context, id + "F28", {"entities" : qUnion([Q0]), "operationType" : NewBodyOperationType.REMOVE, "depth" : 10 * mm, "hasSecondDirection" : true, "secondDirectionOppositeDirection" : false, "secondDirectionDepth" : 6 * mm});
        }
        {
            var Q0;
            Q0=makeQuery(id+"F24.opExtrude","CAP_FACE",FACE,{"disambiguationData":[OSD([sQuery(id+"F23.wireOp",EDGE,"E135.bottom"),sQuery(id+"F23.wireOp",EDGE,"E135.left"),sQuery(id+"F23.wireOp",EDGE,"E135.right"),sQuery(id+"F23.wireOp",EDGE,"E136")])],"isStart":false});
            var sketch = newSketch(context, id + "F29", { "sketchPlane" : qUnion([Q0])});
            skLineSegment(sketch, "E173.bottom", {"start": v(-10, 27) * mm, "end": v(10, 27) * mm});
            skLineSegment(sketch, "E173.top", {"start": v(-10, 17) * mm, "end": v(10, 17) * mm});
            skLineSegment(sketch, "E173.left", {"start": v(-10, 27) * mm, "end": v(-10, 17) * mm});
            skLineSegment(sketch, "E173.right", {"start": v(10, 27) * mm, "end": v(10, 17) * mm});
            skPoint(sketch, "E174", {"position": v(6, 22) * mm});
            skPoint(sketch, "E175", {"position": v(10, 22) * mm});
            skCircle(sketch, "E176", {"center": v(-6, 22) * mm, "radius": 2 * mm});
            skCircle(sketch, "E177", {"center": v(6, 22) * mm, "radius": 2 * mm});
            skSolve(sketch);
        }
        {
            var Q0;
            Q0 = qSketchRegion(id + "F29", true);
            extrude(context, id + "F30", {"entities" : qUnion([Q0]), "depth" : 6 * mm, "hasSecondDirection" : true, "secondDirectionOppositeDirection" : false, "secondDirectionDepth" : 2 * mm});
        }
        {
            var Q0;
            Q0=makeQuery(id+"F30.opExtrude","SWEPT_FACE",FACE,{"disambiguationData":[OSD([sQuery(id+"F29.wireOp",EDGE,"E173.bottom")])]});
            var sketch = newSketch(context, id + "F31", { "sketchPlane" : qUnion([Q0])});
            skLineSegment(sketch, "E178.bottom", {"start": v(-3.75, -23.47) * mm, "end": v(3.75, -23.47) * mm});
            skLineSegment(sketch, "E178.top", {"start": v(-3.75, -24.5) * mm, "end": v(3.75, -24.5) * mm});
            skLineSegment(sketch, "E178.left", {"start": v(-3.75, -23.47) * mm, "end": v(-3.75, -24.5) * mm});
            skLineSegment(sketch, "E178.right", {"start": v(3.75, -23.47) * mm, "end": v(3.75, -24.5) * mm});
            skPoint(sketch, "E179", {"position": v(0, -24.5) * mm});
            skSolve(sketch);
        }
        {
            var Q0;
            Q0 = qSketchRegion(id + "F31", true);
            extrude(context, id + "F32", {"entities" : qUnion([Q0]), "operationType" : NewBodyOperationType.REMOVE, "oppositeDirection" : true, "depth" : 11.58 * mm});
        }
    });
